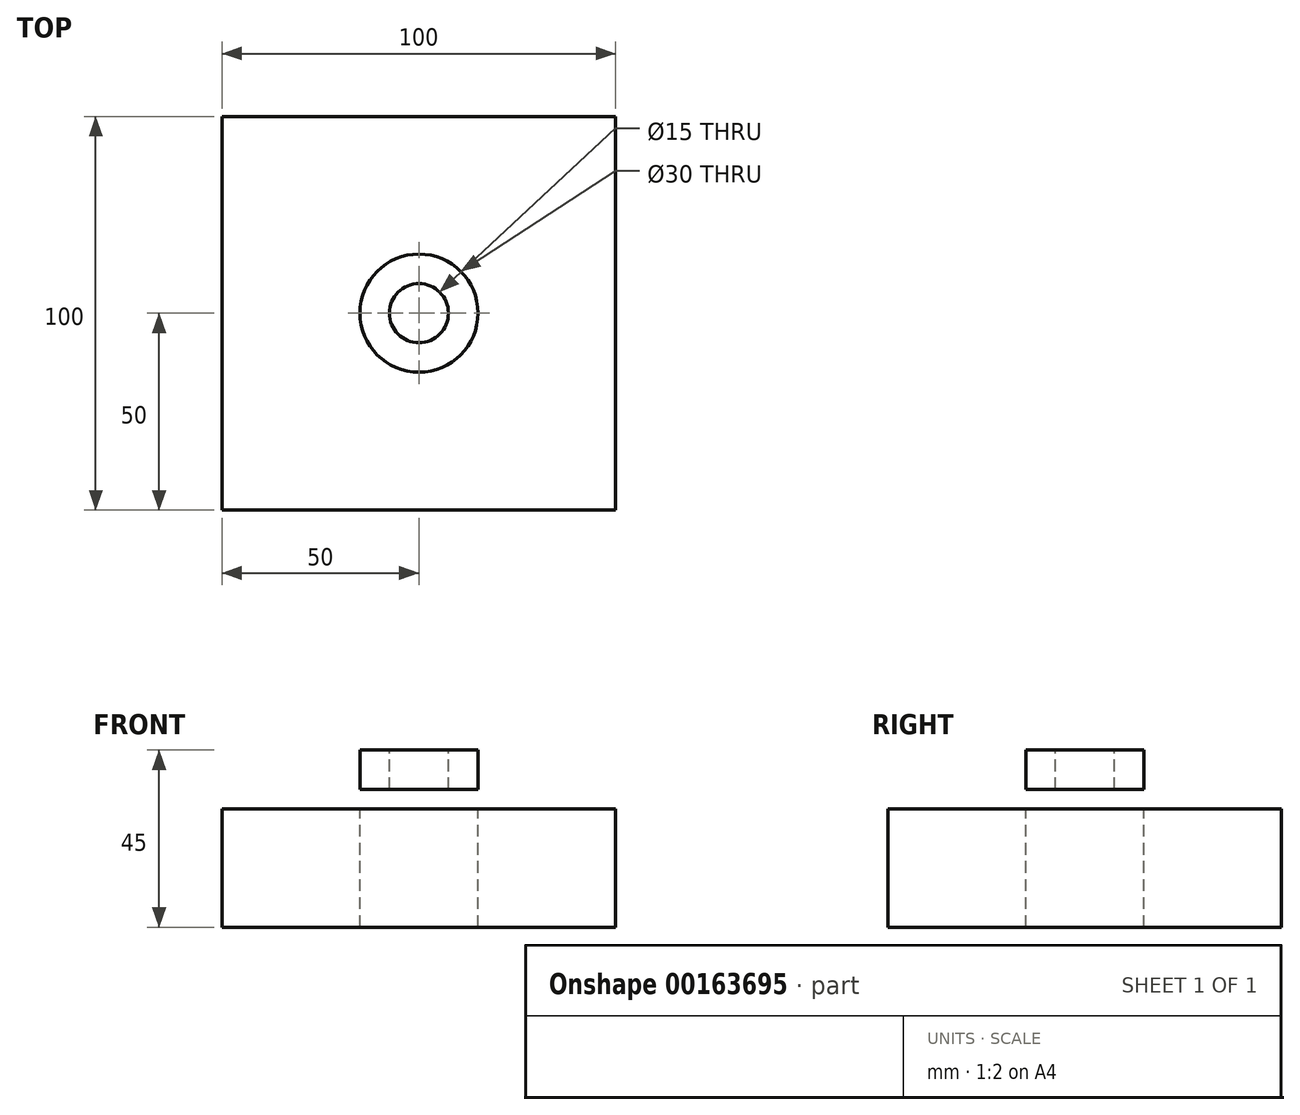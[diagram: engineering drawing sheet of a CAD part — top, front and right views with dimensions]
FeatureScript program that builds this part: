
annotation { "Feature Type Name" : "Feature", "Feature Type Description" : "" }
export const myFeature = defineFeature(function(context is Context, id is Id, definition is map)
    precondition{}
    {
        {
            var Q0;
            Q0=qCreatedBy(makeId("Top.planeOp"),FACE);
            var sketch = newSketch(context, id + "F0", { "sketchPlane" : qUnion([Q0])});
            skLineSegment(sketch, "E0.bottom", {"start": v(50, -50) * mm, "end": v(-50, -50) * mm});
            skLineSegment(sketch, "E0.top", {"start": v(50, 50) * mm, "end": v(-50, 50) * mm});
            skLineSegment(sketch, "E0.left", {"start": v(50, -50) * mm, "end": v(50, 50) * mm});
            skLineSegment(sketch, "E0.right", {"start": v(-50, -50) * mm, "end": v(-50, 50) * mm});
            skPoint(sketch, "E0.middle", {"position": v(0, 0) * mm});
            skSolve(sketch);
        }
        {
            var Q0;
            Q0 = qSketchRegion(id + "F0", true);
            extrude(context, id + "F1", {"entities" : qUnion([Q0]), "oppositeDirection" : true, "depth" : 30 * mm});
        }
        {
            var Q0;
            Q0=makeQuery(id+"F1.opExtrude","CAP_FACE",FACE,{"disambiguationData":[OSD([sQuery(id+"F0.wireOp",EDGE,"E0.bottom"),sQuery(id+"F0.wireOp",EDGE,"E0.top"),sQuery(id+"F0.wireOp",EDGE,"E0.left"),sQuery(id+"F0.wireOp",EDGE,"E0.right")])],"isStart":true});
            var sketch = newSketch(context, id + "F2", { "sketchPlane" : qUnion([Q0])});
            skCircle(sketch, "E1", {"center": v(0, 0) * mm, "radius": 15 * mm});
            skSolve(sketch);
        }
        {
            var Q0;
            Q0 = qSketchRegion(id + "F2", true);
            extrude(context, id + "F3", {"entities" : qUnion([Q0]), "operationType" : NewBodyOperationType.REMOVE, "endBound" : BoundingType.THROUGH_ALL, "oppositeDirection" : true, "depth" : 25 * mm});
        }
        {
            var Q0;
            Q0=qCreatedBy(makeId("Top.planeOp"),FACE);
            var sketch = newSketch(context, id + "F4", { "sketchPlane" : qUnion([Q0])});
            skCircle(sketch, "E2", {"center": v(0, 0) * mm, "radius": 15 * mm});
            skCircle(sketch, "E3", {"center": v(0, 0) * mm, "radius": 7.5 * mm});
            skSolve(sketch);
        }
        {
            var Q0;
            Q0 = qSketchRegion(id + "F4", true);
            extrude(context, id + "F5", {"entities" : qUnion([Q0]), "oppositeDirection" : true, "depth" : 10 * mm});
        }
        {
            var Q0;
            Q0=makeQuery(id+"F5.opExtrude","SWEPT_BODY",BODY,{"disambiguationData":[OSD([sQuery(id+"F4.wireOp",EDGE,"E2"),sQuery(id+"F4.wireOp",EDGE,"E3")])]});
            transform(context, id + "F6", {"entities" : qUnion([Q0]), "transformType" : TransformType.TRANSLATION_3D, "dx" : 0 * mm, "dy" : 0 * mm, "dz" : 15 * mm, "makeCopy" : false});
        }
    });
